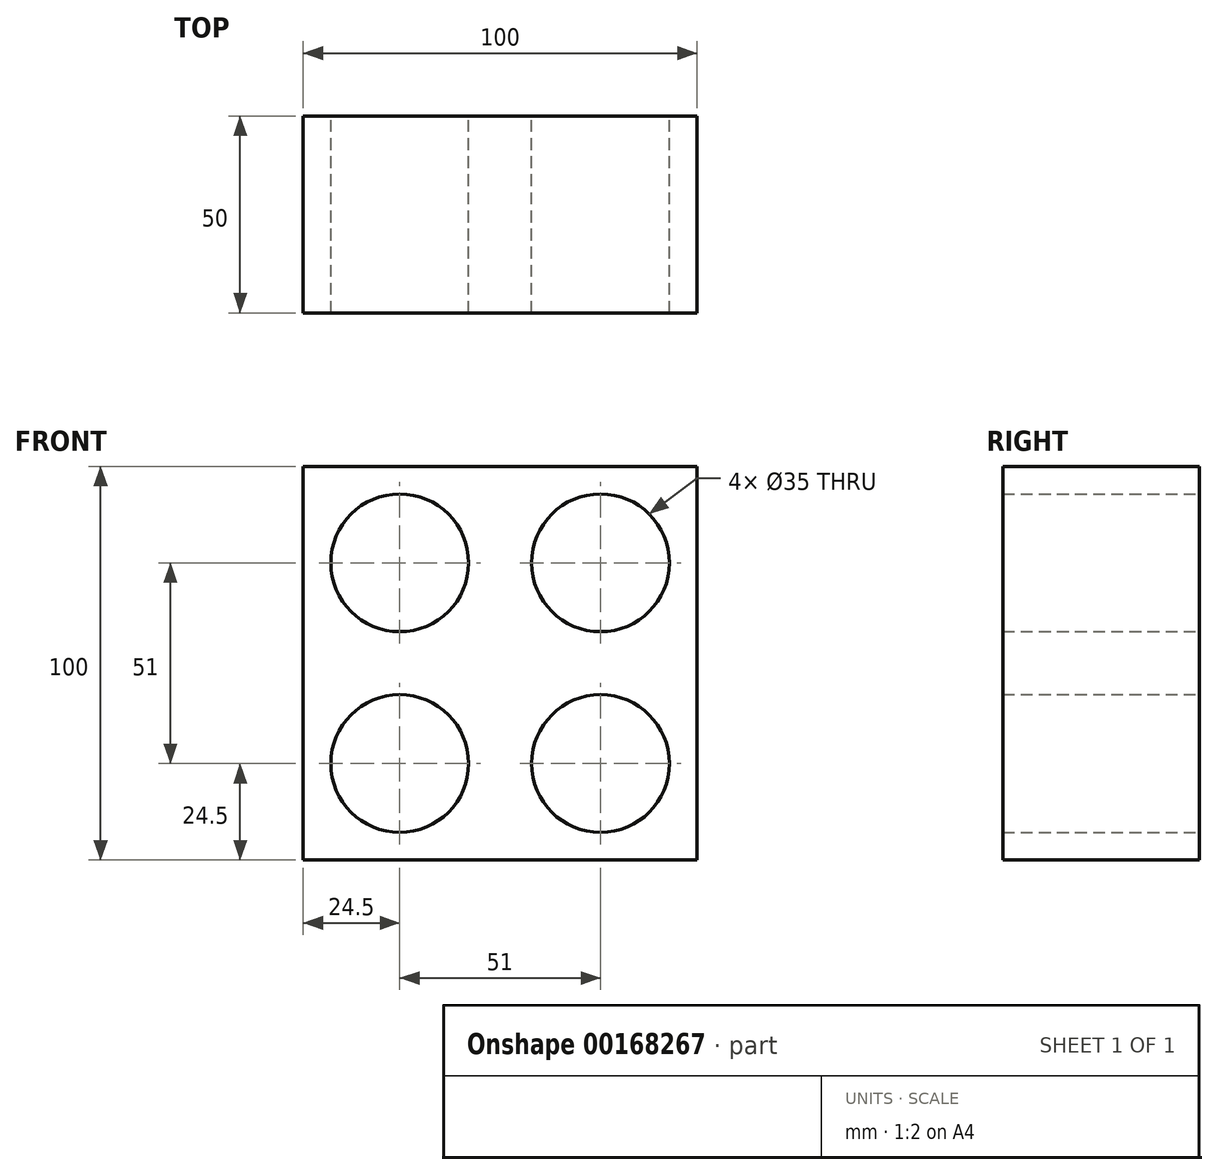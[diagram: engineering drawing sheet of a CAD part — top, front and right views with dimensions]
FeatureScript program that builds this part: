
annotation { "Feature Type Name" : "Feature", "Feature Type Description" : "" }
export const myFeature = defineFeature(function(context is Context, id is Id, definition is map)
    precondition{}
    {
        {
            var Q0;
            Q0=qCreatedBy(makeId("Front.planeOp"),FACE);
            var sketch = newSketch(context, id + "F0", { "sketchPlane" : qUnion([Q0])});
            skLineSegment(sketch, "E0.bottom", {"start": v(-50, 50) * mm, "end": v(50, 50) * mm});
            skLineSegment(sketch, "E0.top", {"start": v(-50, -50) * mm, "end": v(50, -50) * mm});
            skLineSegment(sketch, "E0.left", {"start": v(-50, 50) * mm, "end": v(-50, -50) * mm});
            skLineSegment(sketch, "E0.right", {"start": v(50, 50) * mm, "end": v(50, -50) * mm});
            skPoint(sketch, "E0.middle", {"position": v(0, 0) * mm});
            skCircle(sketch, "E1", {"center": v(-25.5, 25.5) * mm, "radius": 17.5 * mm});
            skCircle(sketch, "E2", {"center": v(25.5, 25.5) * mm, "radius": 17.5 * mm});
            skCircle(sketch, "E3", {"center": v(25.5, -25.5) * mm, "radius": 17.5 * mm});
            skCircle(sketch, "E4", {"center": v(-25.5, -25.5) * mm, "radius": 17.5 * mm});
            skSolve(sketch);
        }
        {
            var Q0;
            Q0=makeQuery(id+"F0.imprint","IMPRINT",FACE,{"disambiguationData":[TD([[makeQuery(id+"F0.imprint","IMPRINT",EDGE,{"derivedFrom":sQuery(id+"F0.wireOp",EDGE,"E0.bottom")}),-1.0]])]});
            extrude(context, id + "F1", {"entities" : qUnion([Q0]), "depth" : 50 * mm});
        }
    });
